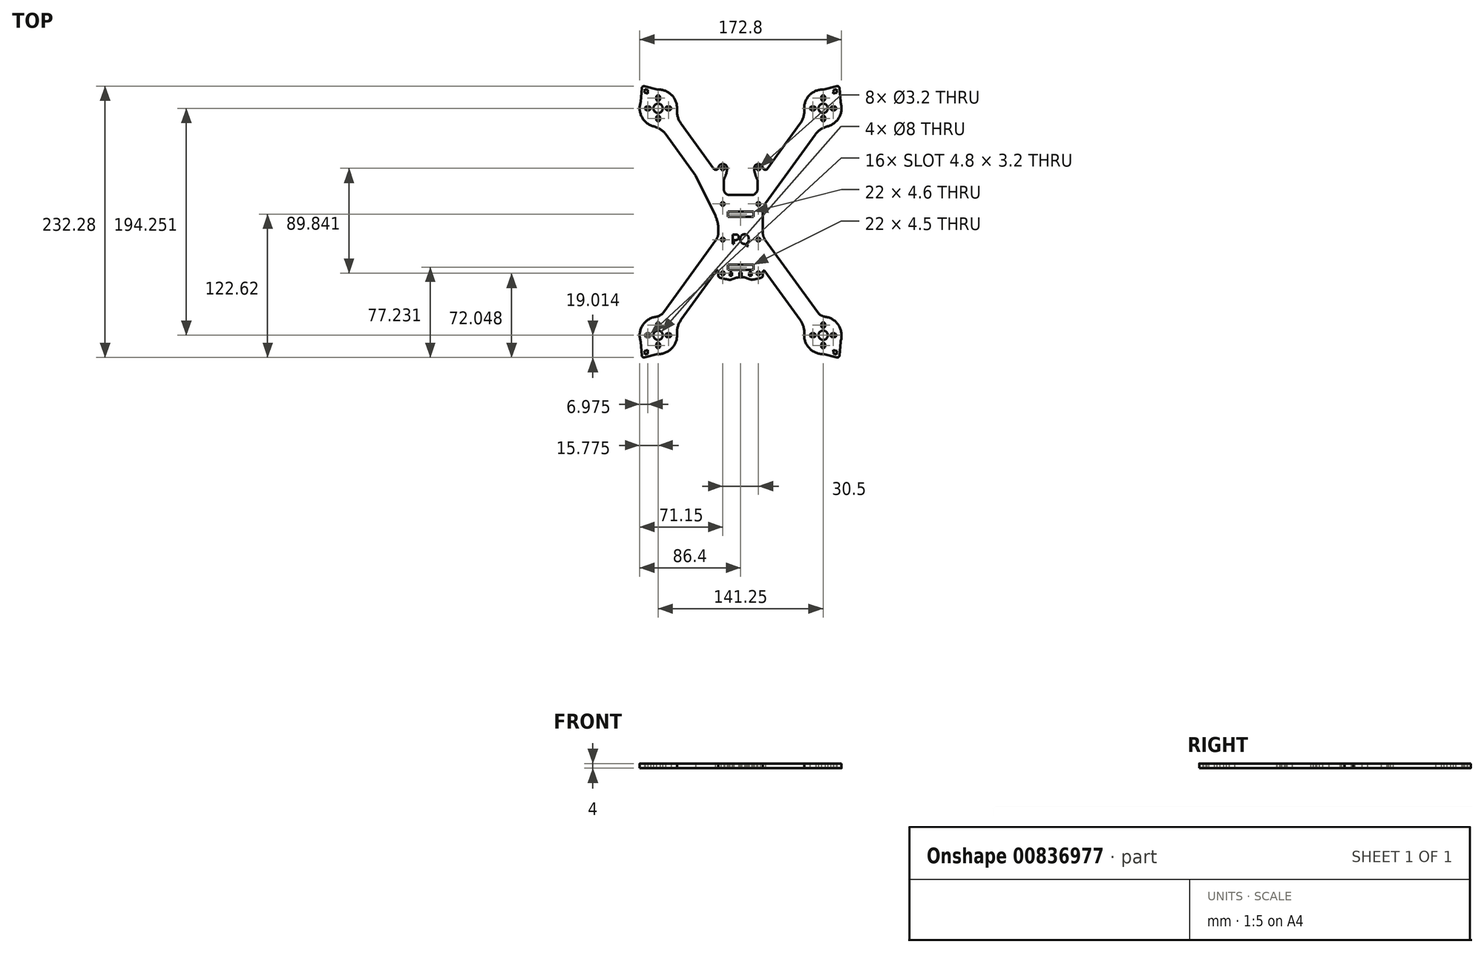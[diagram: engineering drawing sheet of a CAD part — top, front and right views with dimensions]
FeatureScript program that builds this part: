
annotation { "Feature Type Name" : "Feature", "Feature Type Description" : "" }
export const myFeature = defineFeature(function(context is Context, id is Id, definition is map)
    precondition{}
    {
        {
            var Q0;
            Q0=qCreatedBy(makeId("Top.planeOp"),FACE);
            var sketch = newSketch(context, id + "F0", { "sketchPlane" : qUnion([Q0])});
            skPoint(sketch, "E0.middle", {"position": v(0, 0) * mm});
            skPoint(sketch, "E1.middle", {"position": v(0, 44.02) * mm});
            skPoint(sketch, "E1.middle.positionSnap0", {"position": v(0, 20) * mm});
            skPoint(sketch, "E1.centerSnap0", {"position": v(0, 20) * mm});
            skLineSegment(sketch, "E2.0", {"start": v(-19.05, 59.27) * mm, "end": v(-19.05, 53.45) * mm});
            skLineSegment(sketch, "E3", {"start": v(19.05, 28.77) * mm, "end": v(19.05, -1.73) * mm});
            skLineSegment(sketch, "E4.left", {"start": v(-19.05, 28.77) * mm, "end": v(-19.05, 21.4) * mm});
            skCircle(sketch, "E5", {"center": v(15.25, 59.27) * mm, "radius": 1.6 * mm});
            skCircle(sketch, "E6", {"center": v(-15.25, 59.27) * mm, "radius": 1.6 * mm});
            skCircle(sketch, "E7", {"center": v(-15.25, 28.77) * mm, "radius": 1.6 * mm});
            skCircle(sketch, "E8", {"center": v(15.25, 28.77) * mm, "radius": 1.6 * mm});
            skArc(sketch, "E9", {"start": v(-11.5, 59.27) * mm, "mid": v(-15.15, 63.04) * mm, "end": v(-19.04, 59.51) * mm});
            skLineSegment(sketch, "E10", {"start": v(0, 44.02) * mm, "end": v(0, 35.01) * mm});
            skArc(sketch, "E11.MirrorCS", {"start": v(11.5, 59.27) * mm, "mid": v(15.27, 63.04) * mm, "end": v(19.05, 59.27) * mm});
            skLineSegment(sketch, "E12", {"start": v(-11.5, 36.42) * mm, "end": v(11.5, 36.42) * mm});
            skLineSegment(sketch, "E13.bottom", {"start": v(11, 22.3) * mm, "end": v(-11, 22.3) * mm});
            skLineSegment(sketch, "E13.top", {"start": v(11, 17.7) * mm, "end": v(-11, 17.7) * mm});
            skLineSegment(sketch, "E13.left", {"start": v(11, 22.3) * mm, "end": v(11, 17.7) * mm});
            skLineSegment(sketch, "E13.right", {"start": v(-11, 22.3) * mm, "end": v(-11, 17.7) * mm});
            skLineSegment(sketch, "E14.bottom", {"start": v(11, -23.14) * mm, "end": v(-11, -23.14) * mm});
            skLineSegment(sketch, "E14.top", {"start": v(11, -27.64) * mm, "end": v(-11, -27.64) * mm});
            skLineSegment(sketch, "E14.left", {"start": v(11, -23.14) * mm, "end": v(11, -27.64) * mm});
            skLineSegment(sketch, "E14.right", {"start": v(-11, -23.14) * mm, "end": v(-11, -27.64) * mm});
            skPoint(sketch, "E14.middle", {"position": v(0, -25.39) * mm});
            skLineSegment(sketch, "E15.bottom", {"start": v(-15.25, 28.77) * mm, "end": v(-13.65, 28.77) * mm});
            skCircle(sketch, "E16", {"center": v(-15.25, -1.73) * mm, "radius": 1.6 * mm});
            skCircle(sketch, "E17", {"center": v(15.25, -1.73) * mm, "radius": 1.6 * mm});
            skLineSegment(sketch, "E18.trimOffspring", {"start": v(13.65, 28.77) * mm, "end": v(15.25, 28.77) * mm});
            skPoint(sketch, "E19.middle", {"position": v(0, 35.01) * mm});
            skLineSegment(sketch, "E20", {"start": v(40, -23.14) * mm, "end": v(40, -20) * mm});
            skLineSegment(sketch, "E21", {"start": v(-40, -23.14) * mm, "end": v(-40, -20) * mm});
            skArc(sketch, "E22", {"start": v(68.75, 94.8) * mm, "mid": v(82.9, 100.73) * mm, "end": v(85.56, 115.84) * mm});
            skArc(sketch, "E23", {"start": v(72.23, 120.15) * mm, "mid": v(70.63, 121.75) * mm, "end": v(69.03, 120.15) * mm});
            skArc(sketch, "E24", {"start": v(62.63, 109.05) * mm, "mid": v(64.23, 110.65) * mm, "end": v(62.63, 112.25) * mm});
            skArc(sketch, "E25", {"start": v(69.03, 101.15) * mm, "mid": v(70.63, 99.55) * mm, "end": v(72.23, 101.15) * mm});
            skArc(sketch, "E26.trimOffspring", {"start": v(54.66, 113.55) * mm, "mid": v(55, 115.03) * mm, "end": v(55.47, 116.46) * mm});
            skCircle(sketch, "E27", {"center": v(70.63, 110.65) * mm, "radius": 4 * mm});
            skPoint(sketch, "E28", {"position": v(81.36, 110.65) * mm});
            skPoint(sketch, "E29", {"position": v(61.03, 110.65) * mm});
            skPoint(sketch, "E30", {"position": v(80.23, 110.65) * mm});
            skPoint(sketch, "E31", {"position": v(70.63, 118.55) * mm});
            skPoint(sketch, "E32", {"position": v(70.63, 102.75) * mm});
            skArc(sketch, "E33", {"start": v(69.03, 118.55) * mm, "mid": v(70.63, 116.95) * mm, "end": v(72.23, 118.55) * mm});
            skArc(sketch, "E34", {"start": v(61.03, 112.25) * mm, "mid": v(59.43, 110.65) * mm, "end": v(61.03, 109.05) * mm});
            skArc(sketch, "E35", {"start": v(72.23, 102.75) * mm, "mid": v(70.63, 104.35) * mm, "end": v(69.03, 102.75) * mm});
            skPoint(sketch, "E36", {"position": v(62.63, 109.05) * mm});
            skPoint(sketch, "E37", {"position": v(62.63, 112.25) * mm});
            skPoint(sketch, "E38", {"position": v(61.03, 109.05) * mm});
            skPoint(sketch, "E39", {"position": v(61.03, 112.25) * mm});
            skLineSegment(sketch, "E40", {"start": v(61.03, 112.25) * mm, "end": v(62.63, 112.25) * mm});
            skLineSegment(sketch, "E41", {"start": v(62.63, 109.05) * mm, "end": v(61.03, 109.05) * mm});
            skPoint(sketch, "E42.start.orphan", {"position": v(58.93, 110.65) * mm});
            skPoint(sketch, "E43", {"position": v(69.03, 102.75) * mm});
            skPoint(sketch, "E44", {"position": v(72.23, 102.75) * mm});
            skPoint(sketch, "E45", {"position": v(72.23, 101.15) * mm});
            skPoint(sketch, "E46", {"position": v(69.03, 101.15) * mm});
            skLineSegment(sketch, "E47", {"start": v(69.03, 102.75) * mm, "end": v(69.03, 101.15) * mm});
            skLineSegment(sketch, "E48", {"start": v(72.23, 101.15) * mm, "end": v(72.23, 102.75) * mm});
            skPoint(sketch, "E49", {"position": v(78.63, 112.25) * mm});
            skPoint(sketch, "E50", {"position": v(78.63, 109.05) * mm});
            skPoint(sketch, "E51", {"position": v(77.03, 112.25) * mm});
            skPoint(sketch, "E52", {"position": v(77.03, 109.05) * mm});
            skPoint(sketch, "E53", {"position": v(72.23, 120.15) * mm});
            skPoint(sketch, "E54", {"position": v(72.23, 118.55) * mm});
            skPoint(sketch, "E55", {"position": v(69.03, 118.55) * mm});
            skPoint(sketch, "E56", {"position": v(69.03, 120.15) * mm});
            skLineSegment(sketch, "E57", {"start": v(69.03, 120.15) * mm, "end": v(69.03, 118.55) * mm});
            skLineSegment(sketch, "E58", {"start": v(72.23, 120.15) * mm, "end": v(72.23, 118.55) * mm});
            skArc(sketch, "E59", {"start": v(78.63, 112.25) * mm, "mid": v(77.03, 110.65) * mm, "end": v(78.63, 109.05) * mm});
            skArc(sketch, "E60", {"start": v(80.23, 109.05) * mm, "mid": v(81.83, 110.65) * mm, "end": v(80.23, 112.25) * mm});
            skPoint(sketch, "E61", {"position": v(80.23, 112.25) * mm});
            skPoint(sketch, "E62", {"position": v(80.23, 109.05) * mm});
            skLineSegment(sketch, "E63", {"start": v(78.63, 112.25) * mm, "end": v(80.23, 112.25) * mm});
            skLineSegment(sketch, "E64", {"start": v(78.63, 109.05) * mm, "end": v(80.23, 109.05) * mm});
            skLineSegment(sketch, "E65", {"start": v(70.56, 126.7) * mm, "end": v(84.5, 130.18) * mm});
            skLineSegment(sketch, "E66.MirrorCS", {"start": v(85.56, 115.84) * mm, "end": v(84.5, 130.18) * mm});
            skPoint(sketch, "E67.orphan", {"position": v(62.77, 124.77) * mm});
            skPoint(sketch, "E68.orphan", {"position": v(86.14, 107.84) * mm});
            skArc(sketch, "E69.trimOffspring", {"start": v(70.56, 126.7) * mm, "mid": v(57.02, 119.48) * mm, "end": v(55.8, 104.18) * mm});
            skLineSegment(sketch, "E70", {"start": v(82.12, 126.89) * mm, "end": v(82.31, 124.31) * mm});
            skLineSegment(sketch, "E71", {"start": v(82.31, 124.31) * mm, "end": v(79.42, 123.16) * mm});
            skLineSegment(sketch, "E72.MirrorCS", {"start": v(82.12, 126.89) * mm, "end": v(79.61, 126.26) * mm});
            skLineSegment(sketch, "E73.MirrorCS", {"start": v(79.61, 126.26) * mm, "end": v(79.42, 123.16) * mm});
            skPoint(sketch, "E74", {"position": v(0, 27.16) * mm});
            skPoint(sketch, "E74.positionSnap0", {"position": v(0, 36.42) * mm});
            skLineSegment(sketch, "E75.bottom", {"start": v(1, -29.76) * mm, "end": v(-1, -29.76) * mm});
            skLineSegment(sketch, "E75.top", {"start": v(1, -32.76) * mm, "end": v(-1, -32.76) * mm});
            skLineSegment(sketch, "E75.left", {"start": v(1, -29.76) * mm, "end": v(1, -32.76) * mm});
            skLineSegment(sketch, "E75.right", {"start": v(-1, -29.76) * mm, "end": v(-1, -32.76) * mm});
            skPoint(sketch, "E75.middle", {"position": v(0, -31.26) * mm});
            skPoint(sketch, "E75.middle.positionSnap0", {"position": v(0, -27.64) * mm});
            skPoint(sketch, "E75.centerSnap0", {"position": v(0, -27.64) * mm});
            skLineSegment(sketch, "E76.MirrorCS", {"start": v(9.3, -29.76) * mm, "end": v(9.3, -32.76) * mm});
            skLineSegment(sketch, "E77.MirrorCS", {"start": v(7.3, -29.76) * mm, "end": v(7.3, -32.76) * mm});
            skLineSegment(sketch, "E78.MirrorCS", {"start": v(7.3, -32.76) * mm, "end": v(9.3, -32.76) * mm});
            skPoint(sketch, "E79.MirrorP", {"position": v(8.3, -31.26) * mm});
            skLineSegment(sketch, "E80.MirrorCS", {"start": v(7.3, -29.76) * mm, "end": v(9.3, -29.76) * mm});
            skLineSegment(sketch, "E81.MirrorCS", {"start": v(-9.3, -32.76) * mm, "end": v(-7.3, -32.76) * mm});
            skLineSegment(sketch, "E82.MirrorCS", {"start": v(-7.3, -29.76) * mm, "end": v(-7.3, -32.76) * mm});
            skLineSegment(sketch, "E83.MirrorCS", {"start": v(-9.3, -29.76) * mm, "end": v(-9.3, -32.76) * mm});
            skLineSegment(sketch, "E84.MirrorCS", {"start": v(-9.3, -29.76) * mm, "end": v(-7.3, -29.76) * mm});
            skPoint(sketch, "E85.MirrorP", {"position": v(-8.3, -31.26) * mm});
            skArc(sketch, "E86", {"start": v(-19.05, -33.9) * mm, "mid": v(-13.73, -35.33) * mm, "end": v(-8.3, -36.29) * mm});
            skArc(sketch, "E87", {"start": v(8.8, -36.22) * mm, "mid": v(0.23, -33.88) * mm, "end": v(-8.3, -36.29) * mm});
            skPoint(sketch, "E87.endSnap0", {"position": v(-8.3, -32.76) * mm});
            skArc(sketch, "E88.trimOffspring", {"start": v(8.8, -36.22) * mm, "mid": v(13.97, -35.27) * mm, "end": v(19.05, -33.9) * mm});
            skPoint(sketch, "E89.center.orphan", {"position": v(70.4, -83.67) * mm});
            skText(sketch, "E90", { "text": "PQ", "fontName": "OpenSans-Regular.ttf"});
            skCircle(sketch, "E91", {"center": v(15.25, -30.57) * mm, "radius": 1.6 * mm});
            skCircle(sketch, "E92.MirrorC", {"center": v(-15.25, -30.57) * mm, "radius": 1.6 * mm});
            skArc(sketch, "E93.MirrorCS", {"start": v(-78.63, 112.25) * mm, "mid": v(-77.03, 110.65) * mm, "end": v(-78.63, 109.05) * mm});
            skLineSegment(sketch, "E94.MirrorCS", {"start": v(-78.63, 109.05) * mm, "end": v(-80.23, 109.05) * mm});
            skLineSegment(sketch, "E95.MirrorCS", {"start": v(-72.23, 101.15) * mm, "end": v(-72.23, 102.75) * mm});
            skLineSegment(sketch, "E96.MirrorCS", {"start": v(-62.63, 109.05) * mm, "end": v(-61.03, 109.05) * mm});
            skArc(sketch, "E97.MirrorCS", {"start": v(-72.23, 102.75) * mm, "mid": v(-70.63, 104.35) * mm, "end": v(-69.03, 102.75) * mm});
            skLineSegment(sketch, "E98.MirrorCS", {"start": v(-61.03, 112.25) * mm, "end": v(-62.63, 112.25) * mm});
            skArc(sketch, "E99.MirrorCS", {"start": v(-62.63, 109.05) * mm, "mid": v(-64.23, 110.65) * mm, "end": v(-62.63, 112.25) * mm});
            skArc(sketch, "E100.MirrorCS", {"start": v(-69.03, 101.15) * mm, "mid": v(-70.63, 99.55) * mm, "end": v(-72.23, 101.15) * mm});
            skLineSegment(sketch, "E101.MirrorCS", {"start": v(-78.63, 112.25) * mm, "end": v(-80.23, 112.25) * mm});
            skArc(sketch, "E102.MirrorCS", {"start": v(-80.23, 109.05) * mm, "mid": v(-81.83, 110.65) * mm, "end": v(-80.23, 112.25) * mm});
            skArc(sketch, "E103.MirrorCS", {"start": v(-61.03, 112.25) * mm, "mid": v(-59.43, 110.65) * mm, "end": v(-61.03, 109.05) * mm});
            skLineSegment(sketch, "E104.MirrorCS", {"start": v(-69.03, 102.75) * mm, "end": v(-69.03, 101.15) * mm});
            skArc(sketch, "E105.MirrorCS", {"start": v(-69.03, 118.55) * mm, "mid": v(-70.63, 116.95) * mm, "end": v(-72.23, 118.55) * mm});
            skCircle(sketch, "E106.MirrorC", {"center": v(-70.63, 110.65) * mm, "radius": 4 * mm});
            skArc(sketch, "E107.MirrorCS", {"start": v(-72.23, 120.15) * mm, "mid": v(-70.63, 121.75) * mm, "end": v(-69.03, 120.15) * mm});
            skLineSegment(sketch, "E108.MirrorCS", {"start": v(-72.23, 120.15) * mm, "end": v(-72.23, 118.55) * mm});
            skLineSegment(sketch, "E109.MirrorCS", {"start": v(-69.03, 120.15) * mm, "end": v(-69.03, 118.55) * mm});
            skLineSegment(sketch, "E110.MirrorCS", {"start": v(-82.12, 126.89) * mm, "end": v(-79.61, 126.26) * mm});
            skLineSegment(sketch, "E111.MirrorCS", {"start": v(-82.31, 124.31) * mm, "end": v(-79.42, 123.16) * mm});
            skLineSegment(sketch, "E112.MirrorCS", {"start": v(-13.65, 28.77) * mm, "end": v(-15.25, 28.77) * mm});
            skLineSegment(sketch, "E113.MirrorCS", {"start": v(-79.61, 126.26) * mm, "end": v(-79.42, 123.16) * mm});
            skLineSegment(sketch, "E114.MirrorCS", {"start": v(-82.12, 126.89) * mm, "end": v(-82.31, 124.31) * mm});
            skArc(sketch, "E115.MirrorCS", {"start": v(-11.5, 59.27) * mm, "mid": v(-15.27, 63.04) * mm, "end": v(-19.05, 59.27) * mm});
            skLineSegment(sketch, "E116.MirrorCS", {"start": v(-11, 17.7) * mm, "end": v(11, 17.7) * mm});
            skLineSegment(sketch, "E117.MirrorCS", {"start": v(-70.56, 126.7) * mm, "end": v(-84.5, 130.18) * mm});
            skLineSegment(sketch, "E118.MirrorCS", {"start": v(11.5, 36.42) * mm, "end": v(-11.5, 36.42) * mm});
            skArc(sketch, "E119.MirrorCS", {"start": v(-54.66, 113.55) * mm, "mid": v(-55, 115.03) * mm, "end": v(-55.47, 116.46) * mm});
            skLineSegment(sketch, "E120.MirrorCS", {"start": v(-11, 22.3) * mm, "end": v(11, 22.3) * mm});
            skLineSegment(sketch, "E121.MirrorCS", {"start": v(-85.56, 115.84) * mm, "end": v(-84.5, 130.18) * mm});
            skPoint(sketch, "E122.MirrorP", {"position": v(-72.23, 102.75) * mm});
            skPoint(sketch, "E123.MirrorP", {"position": v(-77.03, 112.25) * mm});
            skPoint(sketch, "E124.MirrorP", {"position": v(-72.23, 118.55) * mm});
            skPoint(sketch, "E125.MirrorP", {"position": v(-61.03, 112.25) * mm});
            skPoint(sketch, "E126.MirrorP", {"position": v(-81.36, 110.65) * mm});
            skLineSegment(sketch, "E127.MirrorCS", {"start": v(-19.05, 28.77) * mm, "end": v(-19.05, 26.18) * mm});
            skPoint(sketch, "E128.MirrorP", {"position": v(-78.63, 112.25) * mm});
            skPoint(sketch, "E129.MirrorP", {"position": v(-69.03, 102.75) * mm});
            skArc(sketch, "E130.MirrorCS", {"start": v(-70.56, 126.7) * mm, "mid": v(-57.02, 119.48) * mm, "end": v(-55.8, 104.18) * mm});
            skPoint(sketch, "E131.MirrorP", {"position": v(-69.03, 118.55) * mm});
            skLineSegment(sketch, "E132.MirrorCS", {"start": v(-19.05, 26.18) * mm, "end": v(-21.25, 29.22) * mm});
            skLineSegment(sketch, "E133.MirrorCS", {"start": v(-19.05, 28.77) * mm, "end": v(-19.05, -1.73) * mm});
            skPoint(sketch, "E134.MirrorP", {"position": v(-78.63, 109.05) * mm});
            skPoint(sketch, "E135.MirrorP", {"position": v(-69.03, 101.15) * mm});
            skPoint(sketch, "E136.MirrorP", {"position": v(-86.14, 107.84) * mm});
            skPoint(sketch, "E137.MirrorP", {"position": v(-62.63, 109.05) * mm});
            skPoint(sketch, "E138.MirrorP", {"position": v(-61.03, 109.05) * mm});
            skPoint(sketch, "E139.MirrorP", {"position": v(-72.23, 120.15) * mm});
            skPoint(sketch, "E140.MirrorP", {"position": v(-62.63, 112.25) * mm});
            skPoint(sketch, "E141.MirrorP", {"position": v(-77.03, 109.05) * mm});
            skPoint(sketch, "E142.MirrorP", {"position": v(-58.93, 110.65) * mm});
            skPoint(sketch, "E143.MirrorP", {"position": v(-72.23, 101.15) * mm});
            skPoint(sketch, "E144.MirrorP", {"position": v(-62.77, 124.77) * mm});
            skPoint(sketch, "E145.MirrorP", {"position": v(-80.23, 112.25) * mm});
            skPoint(sketch, "E146.MirrorP", {"position": v(-69.03, 120.15) * mm});
            skArc(sketch, "E147.MirrorCS", {"start": v(-68.75, 94.8) * mm, "mid": v(-82.9, 100.73) * mm, "end": v(-85.56, 115.84) * mm});
            skPoint(sketch, "E148.MirrorP", {"position": v(-80.23, 109.05) * mm});
            skLineSegment(sketch, "E149.MirrorCS", {"start": v(-15.25, -1.73) * mm, "end": v(-13.65, -1.73) * mm});
            skLineSegment(sketch, "E150.MirrorCS", {"start": v(-13.65, -1.73) * mm, "end": v(-15.25, -1.73) * mm});
            skLineSegment(sketch, "E151.MirrorCS", {"start": v(62.63, -82) * mm, "end": v(61.03, -82) * mm});
            skArc(sketch, "E152.MirrorCS", {"start": v(-72.23, -75.7) * mm, "mid": v(-70.63, -77.3) * mm, "end": v(-69.03, -75.7) * mm});
            skArc(sketch, "E153.MirrorCS", {"start": v(62.63, -82) * mm, "mid": v(64.23, -83.6) * mm, "end": v(62.63, -85.2) * mm});
            skArc(sketch, "E154.MirrorCS", {"start": v(72.23, -75.7) * mm, "mid": v(70.63, -77.3) * mm, "end": v(69.03, -75.7) * mm});
            skLineSegment(sketch, "E155.MirrorCS", {"start": v(78.63, -82) * mm, "end": v(80.23, -82) * mm});
            skPoint(sketch, "E156.MirrorP", {"position": v(0, 7.04) * mm});
            skArc(sketch, "E157.MirrorCS", {"start": v(-61.03, -85.2) * mm, "mid": v(-59.43, -83.6) * mm, "end": v(-61.03, -82) * mm});
            skLineSegment(sketch, "E158.MirrorCS", {"start": v(72.23, -74.1) * mm, "end": v(72.23, -75.7) * mm});
            skLineSegment(sketch, "E159.MirrorCS", {"start": v(-72.23, -74.1) * mm, "end": v(-72.23, -75.7) * mm});
            skArc(sketch, "E160.MirrorCS", {"start": v(-62.63, -82) * mm, "mid": v(-64.23, -83.6) * mm, "end": v(-62.63, -85.2) * mm});
            skArc(sketch, "E161.MirrorCS", {"start": v(-69.03, -74.1) * mm, "mid": v(-70.63, -72.5) * mm, "end": v(-72.23, -74.1) * mm});
            skArc(sketch, "E162.MirrorCS", {"start": v(61.03, -85.2) * mm, "mid": v(59.43, -83.6) * mm, "end": v(61.03, -82) * mm});
            skLineSegment(sketch, "E163.MirrorCS", {"start": v(-62.63, -82) * mm, "end": v(-61.03, -82) * mm});
            skArc(sketch, "E164.MirrorCS", {"start": v(78.63, -85.2) * mm, "mid": v(77.03, -83.6) * mm, "end": v(78.63, -82) * mm});
            skLineSegment(sketch, "E165.MirrorCS", {"start": v(78.63, -85.2) * mm, "end": v(80.23, -85.2) * mm});
            skLineSegment(sketch, "E166.MirrorCS", {"start": v(61.03, -85.2) * mm, "end": v(62.63, -85.2) * mm});
            skLineSegment(sketch, "E167.MirrorCS", {"start": v(-69.03, -75.7) * mm, "end": v(-69.03, -74.1) * mm});
            skLineSegment(sketch, "E168.MirrorCS", {"start": v(-61.03, -85.2) * mm, "end": v(-62.63, -85.2) * mm});
            skArc(sketch, "E169.MirrorCS", {"start": v(80.23, -82) * mm, "mid": v(81.83, -83.6) * mm, "end": v(80.23, -85.2) * mm});
            skLineSegment(sketch, "E170.MirrorCS", {"start": v(-78.63, -82) * mm, "end": v(-80.23, -82) * mm});
            skLineSegment(sketch, "E171.MirrorCS", {"start": v(69.03, -75.7) * mm, "end": v(69.03, -74.1) * mm});
            skCircle(sketch, "E172.MirrorC", {"center": v(-70.63, -83.6) * mm, "radius": 4 * mm});
            skLineSegment(sketch, "E173.MirrorCS", {"start": v(-69.03, -93.1) * mm, "end": v(-69.03, -91.5) * mm});
            skLineSegment(sketch, "E174.MirrorCS", {"start": v(69.03, -93.1) * mm, "end": v(69.03, -91.5) * mm});
            skLineSegment(sketch, "E175.MirrorCS", {"start": v(-72.23, -93.1) * mm, "end": v(-72.23, -91.5) * mm});
            skArc(sketch, "E176.MirrorCS", {"start": v(-80.23, -82) * mm, "mid": v(-81.83, -83.6) * mm, "end": v(-80.23, -85.2) * mm});
            skArc(sketch, "E177.MirrorCS", {"start": v(-69.03, -91.5) * mm, "mid": v(-70.63, -89.9) * mm, "end": v(-72.23, -91.5) * mm});
            skArc(sketch, "E178.MirrorCS", {"start": v(-72.23, -93.1) * mm, "mid": v(-70.63, -94.7) * mm, "end": v(-69.03, -93.1) * mm});
            skArc(sketch, "E179.MirrorCS", {"start": v(72.23, -93.1) * mm, "mid": v(70.63, -94.7) * mm, "end": v(69.03, -93.1) * mm});
            skArc(sketch, "E180.MirrorCS", {"start": v(-78.63, -85.2) * mm, "mid": v(-77.03, -83.6) * mm, "end": v(-78.63, -82) * mm});
            skArc(sketch, "E181.MirrorCS", {"start": v(69.03, -74.1) * mm, "mid": v(70.63, -72.5) * mm, "end": v(72.23, -74.1) * mm});
            skCircle(sketch, "E182.MirrorC", {"center": v(70.63, -83.6) * mm, "radius": 4 * mm});
            skLineSegment(sketch, "E183.MirrorCS", {"start": v(-78.63, -85.2) * mm, "end": v(-80.23, -85.2) * mm});
            skArc(sketch, "E184.MirrorCS", {"start": v(69.03, -91.5) * mm, "mid": v(70.63, -89.9) * mm, "end": v(72.23, -91.5) * mm});
            skLineSegment(sketch, "E185.MirrorCS", {"start": v(72.23, -93.1) * mm, "end": v(72.23, -91.5) * mm});
            skLineSegment(sketch, "E186.MirrorCS", {"start": v(79.61, -99.22) * mm, "end": v(79.42, -96.12) * mm});
            skPoint(sketch, "E187.MirrorP", {"position": v(0, -0.12) * mm});
            skLineSegment(sketch, "E188.MirrorCS", {"start": v(-82.12, -99.85) * mm, "end": v(-82.31, -97.27) * mm});
            skLineSegment(sketch, "E189.MirrorCS", {"start": v(-79.61, -99.22) * mm, "end": v(-79.42, -96.12) * mm});
            skLineSegment(sketch, "E190.MirrorCS", {"start": v(0, -16.98) * mm, "end": v(0, -7.98) * mm});
            skLineSegment(sketch, "E191.MirrorCS", {"start": v(13.65, -1.73) * mm, "end": v(15.25, -1.73) * mm});
            skLineSegment(sketch, "E192.MirrorCS", {"start": v(82.31, -97.27) * mm, "end": v(79.42, -96.12) * mm});
            skLineSegment(sketch, "E193.MirrorCS", {"start": v(-82.12, -99.85) * mm, "end": v(-79.61, -99.22) * mm});
            skLineSegment(sketch, "E194.MirrorCS", {"start": v(82.12, -99.85) * mm, "end": v(79.61, -99.22) * mm});
            skLineSegment(sketch, "E195.MirrorCS", {"start": v(-82.31, -97.27) * mm, "end": v(-79.42, -96.12) * mm});
            skLineSegment(sketch, "E196.MirrorCS", {"start": v(82.12, -99.85) * mm, "end": v(82.31, -97.27) * mm});
            skLineSegment(sketch, "E197.MirrorCS", {"start": v(-85.56, -88.8) * mm, "end": v(-84.5, -103.14) * mm});
            skPoint(sketch, "E198.MirrorP", {"position": v(0, 27.04) * mm});
            skArc(sketch, "E199.MirrorCS", {"start": v(54.66, -86.5) * mm, "mid": v(55, -87.99) * mm, "end": v(55.47, -89.42) * mm});
            skLineSegment(sketch, "E200.MirrorCS", {"start": v(85.56, -88.8) * mm, "end": v(84.5, -103.14) * mm});
            skLineSegment(sketch, "E201.MirrorCS", {"start": v(-70.56, -99.67) * mm, "end": v(-84.5, -103.14) * mm});
            skPoint(sketch, "E202.MirrorP", {"position": v(0, -7.98) * mm});
            skLineSegment(sketch, "E203.MirrorCS", {"start": v(-19.05, -1.73) * mm, "end": v(-19.05, 13.52) * mm});
            skPoint(sketch, "E204.MirrorP", {"position": v(81.36, -83.6) * mm});
            skPoint(sketch, "E205.MirrorP", {"position": v(69.03, -91.5) * mm});
            skPoint(sketch, "E206.MirrorP", {"position": v(-69.03, -91.5) * mm});
            skArc(sketch, "E207.MirrorCS", {"start": v(70.56, -99.67) * mm, "mid": v(57.02, -92.44) * mm, "end": v(55.8, -77.14) * mm});
            skPoint(sketch, "E208.MirrorP", {"position": v(78.63, -85.2) * mm});
            skPoint(sketch, "E209.MirrorP", {"position": v(78.63, -82) * mm});
            skPoint(sketch, "E210.MirrorP", {"position": v(72.23, -75.7) * mm});
            skPoint(sketch, "E211.MirrorP", {"position": v(-72.23, -91.5) * mm});
            skLineSegment(sketch, "E212.MirrorCS", {"start": v(-19.05, -32.23) * mm, "end": v(-19.05, -26.42) * mm});
            skArc(sketch, "E213.MirrorCS", {"start": v(-54.66, -86.5) * mm, "mid": v(-55, -87.99) * mm, "end": v(-55.47, -89.42) * mm});
            skLineSegment(sketch, "E214.MirrorCS", {"start": v(-19.05, -1.73) * mm, "end": v(-19.05, 26.18) * mm});
            skLineSegment(sketch, "E215.MirrorCS", {"start": v(70.56, -99.67) * mm, "end": v(84.5, -103.14) * mm});
            skPoint(sketch, "E216.MirrorP", {"position": v(72.23, -91.5) * mm});
            skArc(sketch, "E217.MirrorCS", {"start": v(-70.56, -99.67) * mm, "mid": v(-57.02, -92.44) * mm, "end": v(-55.8, -77.14) * mm});
            skPoint(sketch, "E218.MirrorP", {"position": v(0, -16.98) * mm});
            skPoint(sketch, "E219.MirrorP", {"position": v(-69.03, -75.7) * mm});
            skPoint(sketch, "E220.MirrorP", {"position": v(0, -5.24) * mm});
            skPoint(sketch, "E221.MirrorP", {"position": v(62.63, -85.2) * mm});
            skLineSegment(sketch, "E222.MirrorCS", {"start": v(19.05, -1.73) * mm, "end": v(19.05, 28.77) * mm});
            skPoint(sketch, "E223.MirrorP", {"position": v(-78.63, -82) * mm});
            skPoint(sketch, "E224.MirrorP", {"position": v(77.03, -82) * mm});
            skPoint(sketch, "E225.MirrorP", {"position": v(69.03, -74.1) * mm});
            skPoint(sketch, "E226.MirrorP", {"position": v(61.03, -85.2) * mm});
            skPoint(sketch, "E227.MirrorP", {"position": v(80.23, -82) * mm});
            skPoint(sketch, "E228.MirrorP", {"position": v(-72.23, -93.1) * mm});
            skPoint(sketch, "E229.MirrorP", {"position": v(-72.23, -75.7) * mm});
            skPoint(sketch, "E230.MirrorP", {"position": v(-62.77, -97.73) * mm});
            skLineSegment(sketch, "E231.MirrorCS", {"start": v(6.48, 18.21) * mm, "end": v(6.85, 17.7) * mm});
            skArc(sketch, "E232.MirrorCS", {"start": v(68.75, -67.76) * mm, "mid": v(82.9, -73.69) * mm, "end": v(85.56, -88.8) * mm});
            skLineSegment(sketch, "E233.MirrorCS", {"start": v(20.67, -28.66) * mm, "end": v(55.8, -77.14) * mm});
            skPoint(sketch, "E234.MirrorP", {"position": v(58.93, -83.6) * mm});
            skArc(sketch, "E235.MirrorCS", {"start": v(-68.75, -67.76) * mm, "mid": v(-82.9, -73.69) * mm, "end": v(-85.56, -88.8) * mm});
            skPoint(sketch, "E236.MirrorP", {"position": v(-62.63, -82) * mm});
            skPoint(sketch, "E237.MirrorP", {"position": v(-81.36, -83.6) * mm});
            skLineSegment(sketch, "E238.MirrorCS", {"start": v(19.05, -32.23) * mm, "end": v(19.05, -26.42) * mm});
            skLineSegment(sketch, "E239.MirrorCS", {"start": v(-6.48, 18.21) * mm, "end": v(-6.85, 17.7) * mm});
            skPoint(sketch, "E240.MirrorP", {"position": v(61.03, -82) * mm});
            skPoint(sketch, "E241.MirrorP", {"position": v(86.14, -80.8) * mm});
            skPoint(sketch, "E242.MirrorP", {"position": v(-69.03, -74.1) * mm});
            skPoint(sketch, "E243.MirrorP", {"position": v(80.23, -85.2) * mm});
            skLineSegment(sketch, "E244.MirrorCS", {"start": v(-20.67, -28.66) * mm, "end": v(-55.8, -77.14) * mm});
            skPoint(sketch, "E245.MirrorP", {"position": v(-58.93, -83.6) * mm});
            skPoint(sketch, "E246.MirrorP", {"position": v(-86.14, -80.8) * mm});
            skPoint(sketch, "E247.MirrorP", {"position": v(72.23, -93.1) * mm});
            skPoint(sketch, "E248.MirrorP", {"position": v(-80.23, -82) * mm});
            skPoint(sketch, "E249.MirrorP", {"position": v(-77.03, -82) * mm});
            skPoint(sketch, "E250.MirrorP", {"position": v(-72.23, -74.1) * mm});
            skPoint(sketch, "E251.MirrorP", {"position": v(-61.03, -85.2) * mm});
            skPoint(sketch, "E252.MirrorP", {"position": v(62.77, -97.73) * mm});
            skPoint(sketch, "E253.MirrorP", {"position": v(-80.23, -85.2) * mm});
            skPoint(sketch, "E254.MirrorP", {"position": v(62.63, -82) * mm});
            skPoint(sketch, "E255.MirrorP", {"position": v(69.03, -75.7) * mm});
            skPoint(sketch, "E256.MirrorP", {"position": v(-61.03, -82) * mm});
            skPoint(sketch, "E257.MirrorP", {"position": v(-78.63, -85.2) * mm});
            skPoint(sketch, "E258.MirrorP", {"position": v(69.03, -93.1) * mm});
            skPoint(sketch, "E259.MirrorP", {"position": v(72.23, -74.1) * mm});
            skPoint(sketch, "E260.MirrorP", {"position": v(-77.03, -85.2) * mm});
            skPoint(sketch, "E261.MirrorP", {"position": v(77.03, -85.2) * mm});
            skPoint(sketch, "E262.MirrorP", {"position": v(-62.63, -85.2) * mm});
            skPoint(sketch, "E263.MirrorP", {"position": v(-69.03, -93.1) * mm});
            skLineSegment(sketch, "E264.MirrorCS", {"start": v(11.5, 36.87) * mm, "end": v(11.5, 32.28) * mm});
            skLineSegment(sketch, "E265.trimOffspring", {"start": v(19.05, 53.45) * mm, "end": v(55.8, 104.18) * mm});
            skLineSegment(sketch, "E266.trimOffspring", {"start": v(-22.83, 58.67) * mm, "end": v(-55.8, 104.18) * mm});
            skLineSegment(sketch, "E267.trimOffspring", {"start": v(19.05, 26.18) * mm, "end": v(68.75, 94.8) * mm});
            skLineSegment(sketch, "E268.trimOffspring", {"start": v(19.05, 0.86) * mm, "end": v(68.75, -67.76) * mm});
            skPoint(sketch, "E269.0.start.orphan", {"position": v(6.48, 8.83) * mm});
            skPoint(sketch, "E270.orphan", {"position": v(-6.48, 8.83) * mm});
            skLineSegment(sketch, "E271.trimOffspring", {"start": v(-19.05, 0.86) * mm, "end": v(-68.75, -67.76) * mm});
            skLineSegment(sketch, "E272.trimOffspring", {"start": v(-19.05, -26.42) * mm, "end": v(-19.05, -33.9) * mm});
            skLineSegment(sketch, "E273.trimOffspring", {"start": v(19.05, -26.42) * mm, "end": v(19.05, -33.9) * mm});
            skLineSegment(sketch, "E274.trimOffspring", {"start": v(-19.05, -29.19) * mm, "end": v(-19.05, -33.9) * mm});
            skLineSegment(sketch, "E275.trimOffspring", {"start": v(19.05, -29.19) * mm, "end": v(19.05, -33.9) * mm});
            skLineSegment(sketch, "E276.trimOffspring", {"start": v(19.05, 53.45) * mm, "end": v(19.05, 59.44) * mm});
            skPoint(sketch, "E277.0.start.orphan", {"position": v(19.05, 59.27) * mm});
            skLineSegment(sketch, "E278.trimOffspring", {"start": v(-19.05, 53.45) * mm, "end": v(-19.05, 59.27) * mm});
            skArc(sketch, "E279", {"start": v(-11.57, 58.53) * mm, "mid": v(-11.52, 58.9) * mm, "end": v(-11.5, 59.27) * mm});
            skLineSegment(sketch, "E280", {"start": v(0, 36.42) * mm, "end": v(-11.5, 36.42) * mm});
            skLineSegment(sketch, "E281", {"start": v(-14.47, 41.23) * mm, "end": v(-14.47, 48.35) * mm});
            skPoint(sketch, "E282.MirrorCS.start.orphan", {"position": v(-11.5, 59.27) * mm});
            skArc(sketch, "E283", {"start": v(-13.94, 50.59) * mm, "mid": v(-12.3, 54.81) * mm, "end": v(-11.5, 59.27) * mm});
            skPoint(sketch, "E284.visualSharp", {"position": v(-14.47, 49.59) * mm});
            skArc(sketch, "E284.filletArc", {"start": v(-13.94, 50.59) * mm, "mid": v(-14.34, 49.5) * mm, "end": v(-14.47, 48.35) * mm});
            skArc(sketch, "E285", {"start": v(-22.58, 58.43) * mm, "mid": v(-20.8, 58) * mm, "end": v(-19.25, 58.96) * mm});
            skPoint(sketch, "E286.visualSharp", {"position": v(-22.74, 58.55) * mm});
            skArc(sketch, "E286.filletArc", {"start": v(-22.83, 58.67) * mm, "mid": v(-22.72, 58.54) * mm, "end": v(-22.58, 58.43) * mm});
            skPoint(sketch, "E287.visualSharp", {"position": v(-19.05, 59.27) * mm});
            skArc(sketch, "E287.filletArc", {"start": v(-19.25, 58.96) * mm, "mid": v(-19.1, 59.22) * mm, "end": v(-19.04, 59.51) * mm});
            skArc(sketch, "E288", {"start": v(-14.47, 41.23) * mm, "mid": v(-13.08, 38.03) * mm, "end": v(-10, 36.42) * mm});
            skArc(sketch, "E289.MirrorCS", {"start": v(19.25, 58.96) * mm, "mid": v(19.1, 59.22) * mm, "end": v(19.04, 59.51) * mm});
            skLineSegment(sketch, "E290.MirrorCS", {"start": v(19.05, 59.27) * mm, "end": v(19.05, 53.45) * mm});
            skArc(sketch, "E291.MirrorCS", {"start": v(11.57, 58.53) * mm, "mid": v(11.52, 58.9) * mm, "end": v(11.5, 59.27) * mm});
            skArc(sketch, "E292.MirrorCS", {"start": v(22.83, 58.67) * mm, "mid": v(22.72, 58.54) * mm, "end": v(22.58, 58.43) * mm});
            skArc(sketch, "E293.MirrorCS", {"start": v(13.94, 50.59) * mm, "mid": v(14.34, 49.5) * mm, "end": v(14.47, 48.35) * mm});
            skLineSegment(sketch, "E294.MirrorCS", {"start": v(19.05, 53.45) * mm, "end": v(19.05, 59.27) * mm});
            skLineSegment(sketch, "E295.MirrorCS", {"start": v(22.83, 58.67) * mm, "end": v(55.8, 104.18) * mm});
            skPoint(sketch, "E296.MirrorP", {"position": v(22.74, 58.55) * mm});
            skLineSegment(sketch, "E297.MirrorCS", {"start": v(19.05, 26.18) * mm, "end": v(21.25, 29.22) * mm});
            skArc(sketch, "E298.MirrorCS", {"start": v(14.47, 41.23) * mm, "mid": v(13.08, 38.03) * mm, "end": v(10, 36.42) * mm});
            skArc(sketch, "E299.MirrorCS", {"start": v(11.5, 59.27) * mm, "mid": v(15.15, 63.04) * mm, "end": v(19.04, 59.51) * mm});
            skPoint(sketch, "E300.MirrorP", {"position": v(14.47, 49.59) * mm});
            skArc(sketch, "E301.MirrorCS", {"start": v(13.94, 50.59) * mm, "mid": v(12.3, 54.81) * mm, "end": v(11.5, 59.27) * mm});
            skArc(sketch, "E302.MirrorCS", {"start": v(22.58, 58.43) * mm, "mid": v(20.8, 58) * mm, "end": v(19.25, 58.96) * mm});
            skPoint(sketch, "E303.MirrorP", {"position": v(11.5, 59.27) * mm});
            skLineSegment(sketch, "E304.MirrorCS", {"start": v(0, 36.42) * mm, "end": v(14.47, 36.42) * mm});
            skLineSegment(sketch, "E305.MirrorCS", {"start": v(14.47, 36.42) * mm, "end": v(14.47, 48.35) * mm});
            skPoint(sketch, "E306.orphan", {"position": v(-14.47, 36.42) * mm});
            skPoint(sketch, "E307.visualSharp", {"position": v(-19.05, -26.42) * mm});
            skArc(sketch, "E307.filletArc", {"start": v(-19.05, -29.19) * mm, "mid": v(-19.67, -28.33) * mm, "end": v(-20.67, -28.66) * mm});
            skPoint(sketch, "E308.visualSharp", {"position": v(19.05, -26.42) * mm});
            skArc(sketch, "E308.filletArc", {"start": v(20.67, -28.66) * mm, "mid": v(19.67, -28.33) * mm, "end": v(19.05, -29.19) * mm});
            skArc(sketch, "E309", {"start": v(-19.05, 21.4) * mm, "mid": v(-19.67, 25.45) * mm, "end": v(-21.25, 29.22) * mm});
            skLineSegment(sketch, "E310", {"start": v(-19.05, 13.52) * mm, "end": v(16.37, 13.52) * mm});
            skArc(sketch, "E311.MirrorCS", {"start": v(19.05, 21.4) * mm, "mid": v(19.67, 25.45) * mm, "end": v(21.25, 29.22) * mm});
            skArc(sketch, "E312.MirrorCS", {"start": v(-19.05, 5.63) * mm, "mid": v(-19.67, 1.59) * mm, "end": v(-21.25, -2.18) * mm});
            skArc(sketch, "E313.MirrorCS", {"start": v(19.05, 5.63) * mm, "mid": v(19.67, 1.59) * mm, "end": v(21.25, -2.18) * mm});
            skLineSegment(sketch, "E314", {"start": v(-38.55, 53.1) * mm, "end": v(-21.76, 19.03) * mm});
            skLineSegment(sketch, "E315.trimOffspring", {"start": v(-38.55, 53.1) * mm, "end": v(-68.75, 94.8) * mm});
            skArc(sketch, "E316", {"start": v(-19.05, 8.26) * mm, "mid": v(-19.9, 13.78) * mm, "end": v(-21.76, 19.03) * mm});
            skLineSegment(sketch, "E317.trimOffspring", {"start": v(-19.05, 13.52) * mm, "end": v(-19.05, -1.73) * mm});
            skLineSegment(sketch, "E318.trimOffspring", {"start": v(-19.05, 21.4) * mm, "end": v(-19.05, 28.77) * mm});
            skLineSegment(sketch, "E319.trimOffspring", {"start": v(-19.05, 21.4) * mm, "end": v(-19.05, 26.18) * mm});
            skLineSegment(sketch, "E320.MirrorCS", {"start": v(38.55, 53.1) * mm, "end": v(21.76, 19.03) * mm});
            skArc(sketch, "E321.MirrorCS", {"start": v(19.05, 8.26) * mm, "mid": v(19.9, 13.78) * mm, "end": v(21.76, 19.03) * mm});
            skLineSegment(sketch, "E322.trimOffspring", {"start": v(38.55, 53.1) * mm, "end": v(68.75, 94.8) * mm});
            const initialGuessF0  = {"E90": [-0.00775, -0.0053, 1, 0, 0.00806]};
            skSetInitialGuess(sketch, initialGuessF0);
            skSolve(sketch);
        }
        {
            var Q0;
            Q0=makeQuery(id+"F0.imprint","IMPRINT",FACE,{"disambiguationData":[TD([[makeQuery(id+"F0.imprint","IMPRINT",EDGE,{"derivedFrom":sQuery(id+"F0.wireOp",EDGE,"E8")}),-1.0]])]});
            var Q1;
            Q1=makeQuery(id+"F0.imprint","IMPRINT",FACE,{"disambiguationData":[TD([[makeQuery(id+"F0.imprint","IMPRINT",EDGE,{"derivedFrom":sQuery(id+"F0.wireOp",EDGE,"E267.trimOffspring")}),-1.0]])]});
            var Q2;
            {var subQ0=sQuery(id+"F0.wireOp",EDGE,"E297.MirrorCS");Q2=makeQuery(id+"F0.imprint","IMPRINT",FACE,{"disambiguationData":[TD([[makeQuery(id+"F0.imprint","IMPRINT",EDGE,{"derivedFrom":subQ0}),-1.0]])]});}
            var Q3;
            {var subQ0=sQuery(id+"F0.wireOp",EDGE,"E298.MirrorCS");var subQ1=sQuery(id+"F0.wireOp",EDGE,"E264.MirrorCS");var subQ2=makeQuery(id+"F0.imprint","INTERSECT",VERTEX,{"derivedFrom":[subQ1,subQ0]});Q3=makeQuery(id+"F0.imprint","IMPRINT",FACE,{"disambiguationData":[TD([[makeQuery(id+"F0.imprint","IMPRINT",EDGE,{"disambiguationData":[TD([[subQ2,-1.0]])],"derivedFrom":subQ1}),1.0]])]});}
            var Q4;
            {var subQ0=sQuery(id+"F0.wireOp",EDGE,"E298.MirrorCS");var subQ1=sQuery(id+"F0.wireOp",EDGE,"E264.MirrorCS");var subQ2=makeQuery(id+"F0.imprint","INTERSECT",VERTEX,{"derivedFrom":[subQ1,subQ0]});Q4=makeQuery(id+"F0.imprint","IMPRINT",FACE,{"disambiguationData":[TD([[makeQuery(id+"F0.imprint","IMPRINT",EDGE,{"disambiguationData":[TD([[subQ2,-1.0]])],"derivedFrom":subQ1}),-1.0]])]});}
            var Q5;
            Q5=makeQuery(id+"F0.imprint","IMPRINT",FACE,{"disambiguationData":[TD([[makeQuery(id+"F0.imprint","IMPRINT",EDGE,{"derivedFrom":sQuery(id+"F0.wireOp",EDGE,"E132.MirrorCS")}),1.0]])]});
            var Q6;
            Q6=makeQuery(id+"F0.imprint","IMPRINT",FACE,{"disambiguationData":[TD([[makeQuery(id+"F0.imprint","IMPRINT",EDGE,{"derivedFrom":sQuery(id+"F0.wireOp",EDGE,"E265.trimOffspring")}),1.0]])]});
            extrude(context, id + "F1", {"entities" : qUnion([Q0, Q1, Q2, Q3, Q4, Q5, Q6]), "depth" : 4 * mm, "offsetDistance" : 25 * mm});
        }
        {
            var Q0;
            Q0=makeQuery(id+"F1.opExtrude","SWEPT_EDGE",EDGE,{"disambiguationData":[OSD([sQuery(id+"F0.wireOp",EDGE,"E222.MirrorCS"),sQuery(id+"F0.wireOp",EDGE,"E268.trimOffspring")])]});
            fillet(context, id + "F2", {"entities" : qUnion([Q0]), "radius" : 10 * mm, "tangentPropagation" : true, "allowEdgeOverflow" : false});
        }
        {
            var Q0;
            Q0=makeQuery(id+"F1.opExtrude","SWEPT_EDGE",EDGE,{"disambiguationData":[OSD([sQuery(id+"F0.wireOp",EDGE,"E271.trimOffspring"),sQuery(id+"F0.wireOp",EDGE,"E317.trimOffspring")])]});
            fillet(context, id + "F3", {"entities" : qUnion([Q0]), "radius" : 10 * mm, "tangentPropagation" : true, "allowEdgeOverflow" : false});
        }
        {
            var Q0;
            Q0=makeQuery(id+"F1.opExtrude","SWEPT_EDGE",EDGE,{"disambiguationData":[OSD([sQuery(id+"F0.wireOp",EDGE,"E86"),sQuery(id+"F0.wireOp",EDGE,"E87")])]});
            var Q1;
            Q1=makeQuery(id+"F1.opExtrude","SWEPT_EDGE",EDGE,{"disambiguationData":[OSD([sQuery(id+"F0.wireOp",EDGE,"E87"),sQuery(id+"F0.wireOp",EDGE,"E88.trimOffspring")])]});
            fillet(context, id + "F4", {"entities" : qUnion([Q0, Q1]), "radius" : 5 * mm, "tangentPropagation" : true, "allowEdgeOverflow" : false});
        }
        {
            var Q0;
            Q0=makeQuery(id+"F1.opExtrude","SWEPT_EDGE",EDGE,{"disambiguationData":[OSD([sQuery(id+"F0.wireOp",EDGE,"E200.MirrorCS"),sQuery(id+"F0.wireOp",EDGE,"E215.MirrorCS")])]});
            fillet(context, id + "F5", {"entities" : qUnion([Q0]), "radius" : 2 * mm, "tangentPropagation" : true, "allowEdgeOverflow" : false});
        }
        {
            var Q0;
            Q0=makeQuery(id+"F1.opExtrude","SWEPT_EDGE",EDGE,{"disambiguationData":[OSD([sQuery(id+"F0.wireOp",EDGE,"E200.MirrorCS"),sQuery(id+"F0.wireOp",EDGE,"E232.MirrorCS")])]});
            var Q1;
            Q1=makeQuery(id+"F1.opExtrude","SWEPT_EDGE",EDGE,{"disambiguationData":[OSD([sQuery(id+"F0.wireOp",EDGE,"E207.MirrorCS"),sQuery(id+"F0.wireOp",EDGE,"E215.MirrorCS")])]});
            fillet(context, id + "F6", {"entities" : qUnion([Q0, Q1]), "radius" : 5 * mm, "tangentPropagation" : true, "allowEdgeOverflow" : false});
        }
        {
            var Q0;
            Q0=makeQuery(id+"F1.opExtrude","SWEPT_EDGE",EDGE,{"disambiguationData":[OSD([sQuery(id+"F0.wireOp",EDGE,"E197.MirrorCS"),sQuery(id+"F0.wireOp",EDGE,"E201.MirrorCS")])]});
            fillet(context, id + "F7", {"entities" : qUnion([Q0]), "radius" : 2 * mm, "tangentPropagation" : true, "allowEdgeOverflow" : false});
        }
        {
            var Q0;
            Q0=makeQuery(id+"F1.opExtrude","SWEPT_EDGE",EDGE,{"disambiguationData":[OSD([sQuery(id+"F0.wireOp",EDGE,"E201.MirrorCS"),sQuery(id+"F0.wireOp",EDGE,"E217.MirrorCS")])]});
            var Q1;
            Q1=makeQuery(id+"F1.opExtrude","SWEPT_EDGE",EDGE,{"disambiguationData":[OSD([sQuery(id+"F0.wireOp",EDGE,"E197.MirrorCS"),sQuery(id+"F0.wireOp",EDGE,"E235.MirrorCS")])]});
            fillet(context, id + "F8", {"entities" : qUnion([Q0, Q1]), "radius" : 5 * mm, "tangentPropagation" : true, "allowEdgeOverflow" : false});
        }
        {
            var Q0;
            Q0=makeQuery(id+"F1.opExtrude","SWEPT_EDGE",EDGE,{"disambiguationData":[OSD([sQuery(id+"F0.wireOp",EDGE,"E117.MirrorCS"),sQuery(id+"F0.wireOp",EDGE,"E121.MirrorCS")])]});
            var Q1;
            Q1=makeQuery(id+"F1.opExtrude","SWEPT_EDGE",EDGE,{"disambiguationData":[OSD([sQuery(id+"F0.wireOp",EDGE,"E65"),sQuery(id+"F0.wireOp",EDGE,"E66.MirrorCS")])]});
            fillet(context, id + "F9", {"entities" : qUnion([Q0, Q1]), "radius" : 2 * mm, "tangentPropagation" : true, "allowEdgeOverflow" : false});
        }
        {
            var Q0;
            Q0=makeQuery(id+"F1.opExtrude","SWEPT_EDGE",EDGE,{"disambiguationData":[OSD([sQuery(id+"F0.wireOp",EDGE,"E22"),sQuery(id+"F0.wireOp",EDGE,"E66.MirrorCS")])]});
            var Q1;
            Q1=makeQuery(id+"F1.opExtrude","SWEPT_EDGE",EDGE,{"disambiguationData":[OSD([sQuery(id+"F0.wireOp",EDGE,"E65"),sQuery(id+"F0.wireOp",EDGE,"E69.trimOffspring")])]});
            var Q2;
            Q2=makeQuery(id+"F1.opExtrude","SWEPT_EDGE",EDGE,{"disambiguationData":[OSD([sQuery(id+"F0.wireOp",EDGE,"E121.MirrorCS"),sQuery(id+"F0.wireOp",EDGE,"E147.MirrorCS")])]});
            var Q3;
            Q3=makeQuery(id+"F1.opExtrude","SWEPT_EDGE",EDGE,{"disambiguationData":[OSD([sQuery(id+"F0.wireOp",EDGE,"E117.MirrorCS"),sQuery(id+"F0.wireOp",EDGE,"E130.MirrorCS")])]});
            fillet(context, id + "F10", {"entities" : qUnion([Q0, Q1, Q2, Q3]), "radius" : 5 * mm, "tangentPropagation" : true, "allowEdgeOverflow" : false});
        }
        {
            var Q0;
            Q0=makeQuery(id+"F1.opExtrude","SWEPT_EDGE",EDGE,{"disambiguationData":[OSD([sQuery(id+"F0.wireOp",EDGE,"E232.MirrorCS"),sQuery(id+"F0.wireOp",EDGE,"E268.trimOffspring")])]});
            var Q1;
            Q1=makeQuery(id+"F1.opExtrude","SWEPT_EDGE",EDGE,{"disambiguationData":[OSD([sQuery(id+"F0.wireOp",EDGE,"E207.MirrorCS"),sQuery(id+"F0.wireOp",EDGE,"E233.MirrorCS")])]});
            fillet(context, id + "F11", {"entities" : qUnion([Q0, Q1]), "radius" : 18 * mm, "tangentPropagation" : true, "allowEdgeOverflow" : false});
        }
        {
            var Q0;
            Q0=makeQuery(id+"F1.opExtrude","SWEPT_EDGE",EDGE,{"disambiguationData":[OSD([sQuery(id+"F0.wireOp",EDGE,"E235.MirrorCS"),sQuery(id+"F0.wireOp",EDGE,"E271.trimOffspring")])]});
            var Q1;
            Q1=makeQuery(id+"F1.opExtrude","SWEPT_EDGE",EDGE,{"disambiguationData":[OSD([sQuery(id+"F0.wireOp",EDGE,"E217.MirrorCS"),sQuery(id+"F0.wireOp",EDGE,"E244.MirrorCS")])]});
            var Q2;
            Q2=makeQuery(id+"F1.opExtrude","SWEPT_EDGE",EDGE,{"disambiguationData":[OSD([sQuery(id+"F0.wireOp",EDGE,"E22"),sQuery(id+"F0.wireOp",EDGE,"E322.trimOffspring")])]});
            var Q3;
            Q3=makeQuery(id+"F1.opExtrude","SWEPT_EDGE",EDGE,{"disambiguationData":[OSD([sQuery(id+"F0.wireOp",EDGE,"E130.MirrorCS"),sQuery(id+"F0.wireOp",EDGE,"E266.trimOffspring")])]});
            var Q4;
            Q4=makeQuery(id+"F1.opExtrude","SWEPT_EDGE",EDGE,{"disambiguationData":[OSD([sQuery(id+"F0.wireOp",EDGE,"E147.MirrorCS"),sQuery(id+"F0.wireOp",EDGE,"E315.trimOffspring")])]});
            var Q5;
            Q5=makeQuery(id+"F1.opExtrude","SWEPT_EDGE",EDGE,{"disambiguationData":[OSD([sQuery(id+"F0.wireOp",EDGE,"E69.trimOffspring"),sQuery(id+"F0.wireOp",EDGE,"E295.MirrorCS")])]});
            fillet(context, id + "F12", {"entities" : qUnion([Q0, Q1, Q2, Q3, Q4, Q5]), "radius" : 18 * mm, "tangentPropagation" : true, "allowEdgeOverflow" : false});
        }
        {
            var Q0;
            Q0=makeQuery(id+"F1.opExtrude","SWEPT_EDGE",EDGE,{"disambiguationData":[OSD([sQuery(id+"F0.wireOp",EDGE,"E88.trimOffspring"),sQuery(id+"F0.wireOp",EDGE,"E275.trimOffspring")])]});
            var Q1;
            Q1=makeQuery(id+"F1.opExtrude","SWEPT_EDGE",EDGE,{"disambiguationData":[OSD([sQuery(id+"F0.wireOp",EDGE,"E86"),sQuery(id+"F0.wireOp",EDGE,"E272.trimOffspring")])]});
            fillet(context, id + "F13", {"entities" : qUnion([Q0, Q1]), "radius" : 2 * mm, "tangentPropagation" : true, "allowEdgeOverflow" : false});
        }
    });
